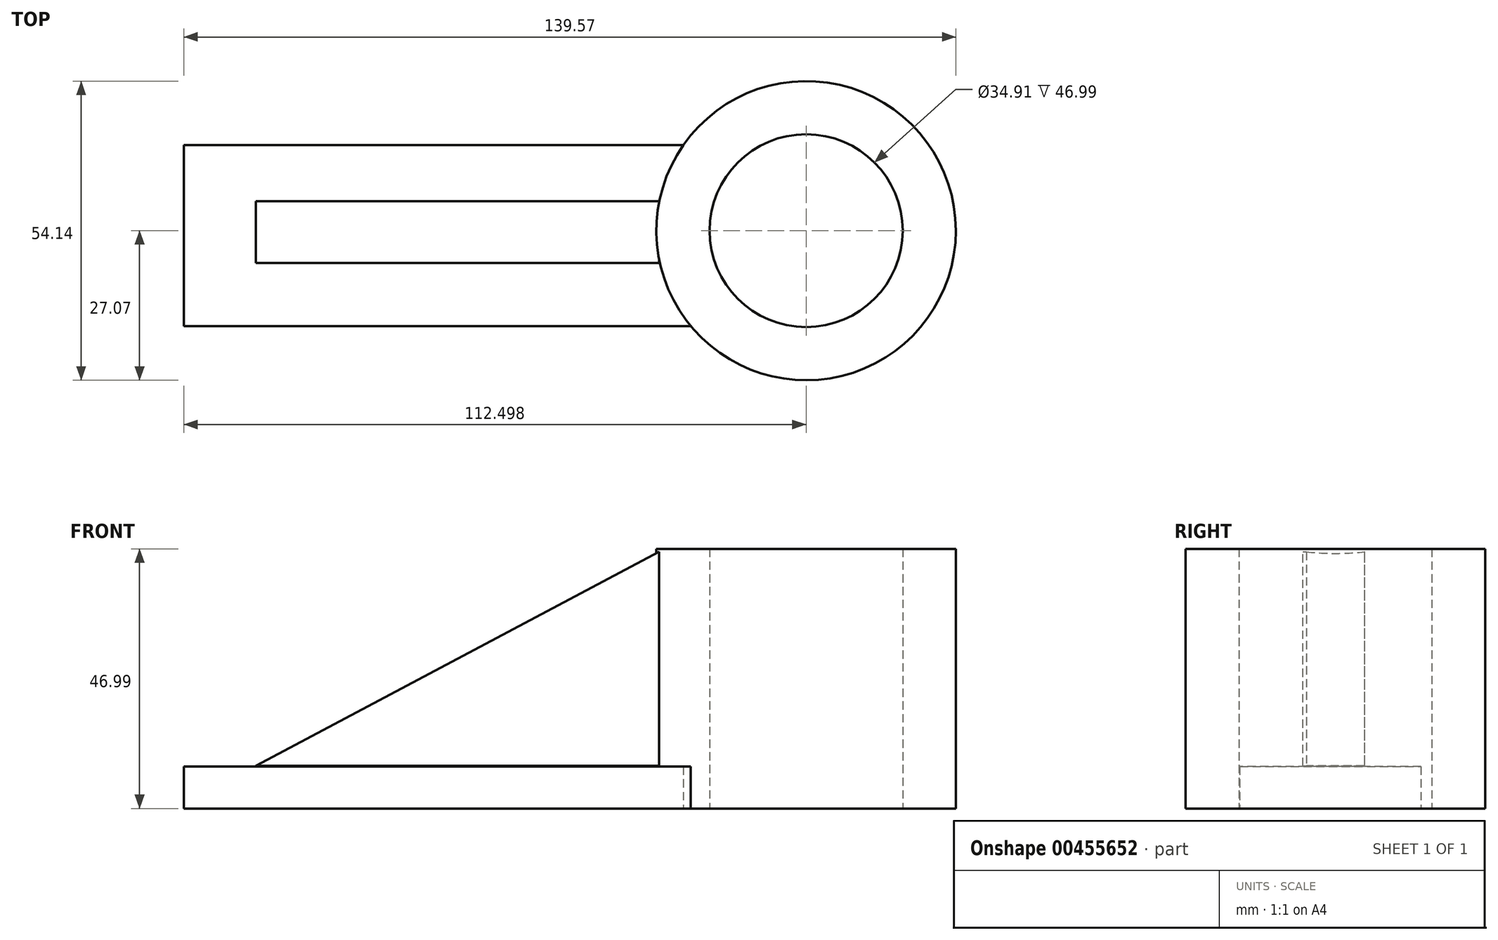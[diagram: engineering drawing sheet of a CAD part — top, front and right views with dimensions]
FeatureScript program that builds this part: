
annotation { "Feature Type Name" : "Feature", "Feature Type Description" : "" }
export const myFeature = defineFeature(function(context is Context, id is Id, definition is map)
    precondition{}
    {
        {
            var Q0;
            Q0=qCreatedBy(makeId("Top.planeOp"),FACE);
            var sketch = newSketch(context, id + "F0", { "sketchPlane" : qUnion([Q0])});
            skLineSegment(sketch, "E0.bottom", {"start": v(-40.99, 21.62) * mm, "end": v(24.7, 21.62) * mm});
            skLineSegment(sketch, "E0.top", {"start": v(-40.99, -21.62) * mm, "end": v(24.7, -21.62) * mm});
            skLineSegment(sketch, "E0.left", {"start": v(-40.99, 21.62) * mm, "end": v(-40.99, -21.62) * mm});
            skPoint(sketch, "E0.middle", {"position": v(0, 0) * mm});
            skCircle(sketch, "E1", {"center": v(40.99, 0) * mm, "radius": 27.07 * mm});
            skCircle(sketch, "E2", {"center": v(40.99, 0) * mm, "radius": 17.46 * mm});
            skSolve(sketch);
        }
        {
            var Q0;
            Q0=makeQuery(id+"F0.imprint","IMPRINT",FACE,{"disambiguationData":[TD([[makeQuery(id+"F0.imprint","IMPRINT",EDGE,{"derivedFrom":sQuery(id+"F0.wireOp",EDGE,"E2")}),-1.0]])]});
            extrude(context, id + "F1", {"entities" : qUnion([Q0]), "depth" : 47 * mm});
        }
        {
            var Q0;
            Q0=qCreatedBy(makeId("Front.planeOp"),FACE);
            var sketch = newSketch(context, id + "F2", { "sketchPlane" : qUnion([Q0])});
            skLineSegment(sketch, "E3.bottom", {"start": v(-71.5, 0) * mm, "end": v(20.85, 0) * mm});
            skLineSegment(sketch, "E3.top", {"start": v(-71.5, 7.58) * mm, "end": v(20.85, 7.58) * mm});
            skLineSegment(sketch, "E3.left", {"start": v(-71.5, 0) * mm, "end": v(-71.5, 7.58) * mm});
            skLineSegment(sketch, "E3.right", {"start": v(20.85, 0) * mm, "end": v(20.85, 7.58) * mm});
            skSolve(sketch);
        }
        {
            var Q0;
            Q0=makeQuery(id+"F2.imprint","IMPRINT",FACE,{"disambiguationData":[TD([[makeQuery(id+"F2.imprint","IMPRINT",EDGE,{"derivedFrom":sQuery(id+"F2.wireOp",EDGE,"E3.bottom")}),1.0]])]});
            extrude(context, id + "F3", {"entities" : qUnion([Q0]), "operationType" : NewBodyOperationType.ADD, "depth" : 17.27 * mm, "hasSecondDirection" : true, "secondDirectionOppositeDirection" : true, "secondDirectionDepth" : 15.5 * mm});
        }
        {
            var Q0;
            Q0=qCreatedBy(makeId("Front.planeOp"),FACE);
            var sketch = newSketch(context, id + "F4", { "sketchPlane" : qUnion([Q0])});
            skLineSegment(sketch, "E4", {"start": v(-58.52, 7.7) * mm, "end": v(14.43, 7.7) * mm});
            skLineSegment(sketch, "E5", {"start": v(14.43, 7.7) * mm, "end": v(14.43, 46.44) * mm});
            skLineSegment(sketch, "E6", {"start": v(14.43, 46.44) * mm, "end": v(-58.52, 7.7) * mm});
            skSolve(sketch);
        }
        {
            var Q0;
            Q0 = qSketchRegion(id + "F4", true);
            extrude(context, id + "F5", {"entities" : qUnion([Q0]), "operationType" : NewBodyOperationType.ADD, "depth" : 5.84 * mm, "hasSecondDirection" : true, "secondDirectionOppositeDirection" : true, "secondDirectionDepth" : 5.33 * mm});
        }
    });
